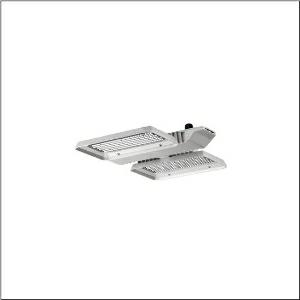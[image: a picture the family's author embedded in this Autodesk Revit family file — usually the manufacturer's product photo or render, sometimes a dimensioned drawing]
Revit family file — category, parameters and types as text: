
# Revit family: highbay_11_51hla2d14fcad
name_source: partatom
category: Lighting Fixtures
units: mm (PartAtom-declared; Revit-internal decimal feet)

## family parameters
Cut with Voids When Loaded = No
Host = Face
Light Source = No
Part Type = Normal
Room Calculation Point = No
Round Connector Dimension = Use Diameter
Shared = No

## types (1)
- --- (1 x LED, 2160 lm, 14 W, 4000K)
    Apparent Load = 14 VA
    CIE Flux Codes = 89 96 99 100 100
    Color Rendering = 80
    Color Temperature = 4000K
    Default Elevation = 1800 mm
    Description = Highbay 11, LED high bay luminaire, primary light control with lens, of PMMA, light emission: direct distribution, primary light characteristic: symmetric, installation type: suspended mounting, surface-mounted, for 1x 2 x LED rated luminous flux: 14.400 lm, light colour: 840, colour temperature: 4000K, control gear: ECG DALI, with terminal, 5-pole, max. 2.5mm², mains connection: 230..240V, AC/DC, 50/60Hz, rated input power: 81W, LED unit, of diecast aluminium, bead blasted, unplated, silver, length: 470 mm, width: 500 mm, height: 65mm, housing, of diecast aluminium, bead blasted, uncoated, silver, protection rating (complete): IP65, insulation class (complete): insulation class I (protective earthing), certification: CE, protection symbol: D, impact resistance: IK08 with glass or PC cover, permissible ambient temperature for indoor applications: -35..+55°C, standard: EN 60598-2-22, reducing of maximum allowable ambient temperature of 5°C with ceiling mounting, corresponds to IFS (International Featured Standards) requirements for safety and quality in the food industry, packaging unit: 1 piece
    Height = 95 mm
    Lamp = 1 x LED
    Lamp Light Flux = 2160 lm
    Lamp Power = 14 W
    Lamp count = 1
    Length = 468 mm
    Luminous efficacy = 154 lm/W
    Manufacturer = Siteco
    ModVariant = No
    Model = 51HLA2D14FCAD
    Mounting Place = Ceiling
    Mounting Type = Pendant
    Number of Poles = 1
    OnlyDefault = Yes
    Power Factor = 1
    Product Name = Highbay 11
    Product group = LED high bay luminaire
    ProductGroupID = 903
    Protection Class = Protection class I
    Protection Degree = IP 65
    RLX_Detail_Level = 1
    RlxData = <blob elided: 86557 chars, md5=d67b006e>
    Socket = socket
    Standby Power = 0 W
    System Light Flux = 2160 lm
    System Power = 14 W
    Type Comments = : central accumulator DC – ECG emengency level 15%
    Type Image = l_1003425.jpg
    URL = http://relux.com
    VarID = @adj_128325
    Voltage = 0 V
    Weight = 0.00 kg
    Width = 501 mm

## geometry (parser evidence)
native form markers: Blend x4, Sweep x15
no freeform markers — native parametric forms only
